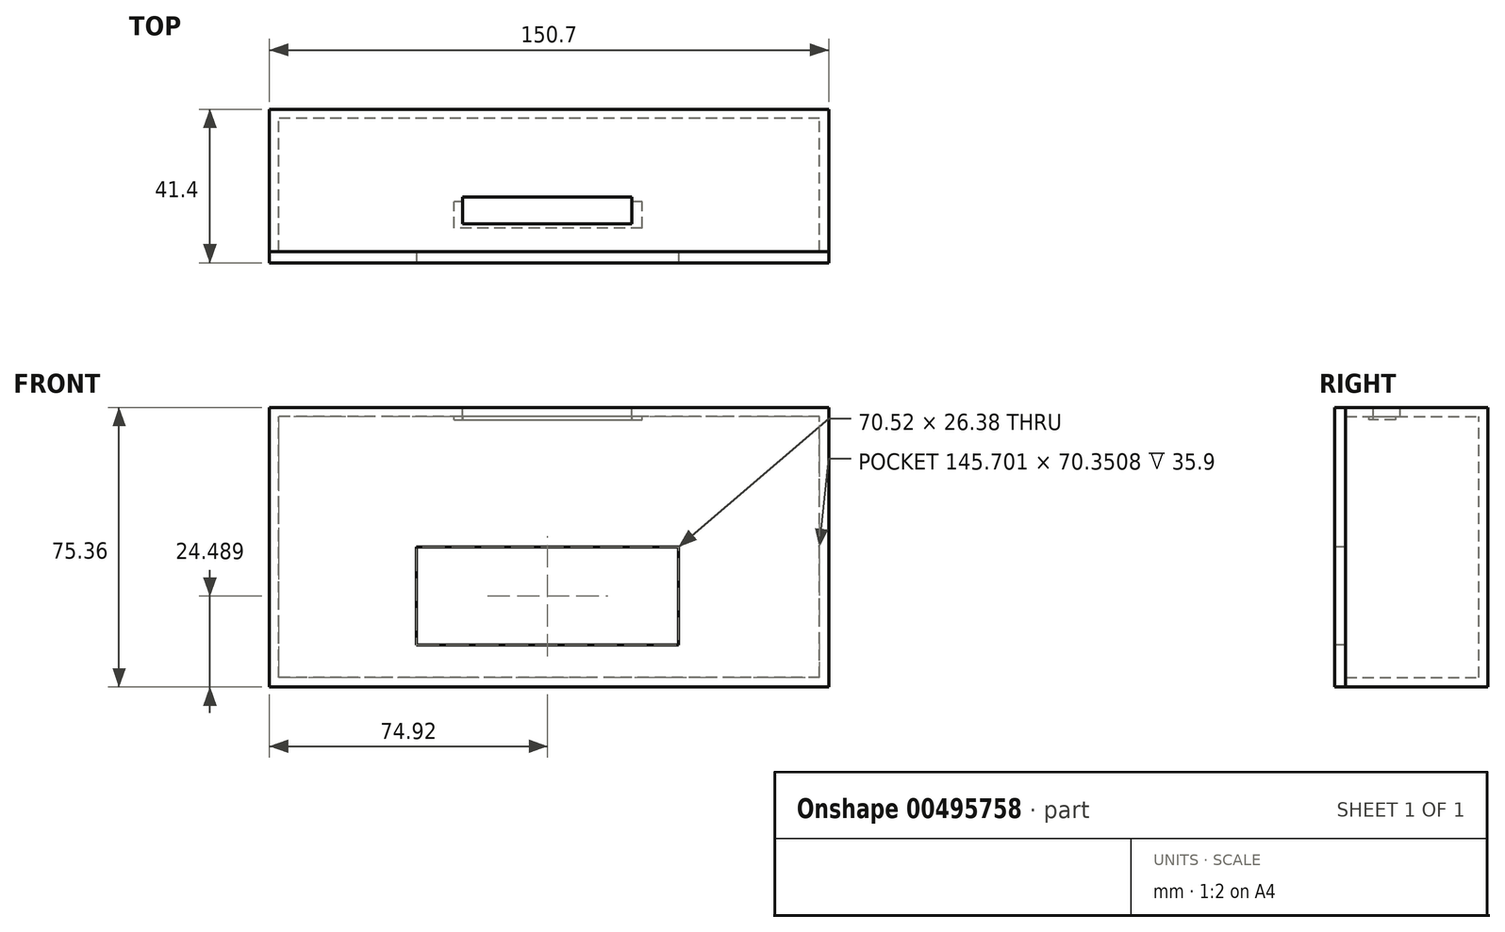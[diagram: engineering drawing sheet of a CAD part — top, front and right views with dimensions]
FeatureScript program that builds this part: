
annotation { "Feature Type Name" : "Feature", "Feature Type Description" : "" }
export const myFeature = defineFeature(function(context is Context, id is Id, definition is map)
    precondition{}
    {
        {
            var Q0;
            Q0=qCreatedBy(makeId("Front.planeOp"),FACE);
            var sketch = newSketch(context, id + "F0", { "sketchPlane" : qUnion([Q0])});
            skLineSegment(sketch, "E0.bottom", {"start": v(75.35, -37.68) * mm, "end": v(-75.35, -37.68) * mm});
            skLineSegment(sketch, "E0.top", {"start": v(75.35, 37.68) * mm, "end": v(-75.35, 37.68) * mm});
            skLineSegment(sketch, "E0.left", {"start": v(75.35, -37.68) * mm, "end": v(75.35, 37.68) * mm});
            skLineSegment(sketch, "E0.right", {"start": v(-75.35, -37.68) * mm, "end": v(-75.35, 37.68) * mm});
            skPoint(sketch, "E0.middle", {"position": v(0, 0) * mm});
            skSolve(sketch);
        }
        {
            var Q0;
            Q0 = qSketchRegion(id + "F0", true);
            extrude(context, id + "F1", {"entities" : qUnion([Q0]), "depth" : 38.4 * mm});
        }
        {
            var Q0;
            Q0=makeQuery(id+"F1.opExtrude","CAP_FACE",FACE,{"disambiguationData":[OSD([sQuery(id+"F0.wireOp",EDGE,"E0.bottom"),sQuery(id+"F0.wireOp",EDGE,"E0.top"),sQuery(id+"F0.wireOp",EDGE,"E0.left"),sQuery(id+"F0.wireOp",EDGE,"E0.right")])],"isStart":false});
            shell(context, id + "F2", {"entities" : qUnion([Q0]), "thickness" : 2.5 * mm});
        }
        {
            var Q0;
            Q0=makeQuery(id+"F1.opExtrude","CAP_FACE",FACE,{"disambiguationData":[OSD([sQuery(id+"F0.wireOp",EDGE,"E0.bottom"),sQuery(id+"F0.wireOp",EDGE,"E0.top"),sQuery(id+"F0.wireOp",EDGE,"E0.left"),sQuery(id+"F0.wireOp",EDGE,"E0.right")])],"isStart":false});
            var sketch = newSketch(context, id + "F3", { "sketchPlane" : qUnion([Q0])});
            skLineSegment(sketch, "E1.bottom", {"start": v(-75.35, 37.68) * mm, "end": v(75.35, 37.68) * mm});
            skLineSegment(sketch, "E1.top", {"start": v(-75.35, -37.68) * mm, "end": v(75.35, -37.68) * mm});
            skLineSegment(sketch, "E1.left", {"start": v(-75.35, 37.68) * mm, "end": v(-75.35, -37.68) * mm});
            skLineSegment(sketch, "E1.right", {"start": v(75.35, 37.68) * mm, "end": v(75.35, -37.68) * mm});
            skSolve(sketch);
        }
        {
            var Q0;
            Q0 = qSketchRegion(id + "F3", true);
            extrude(context, id + "F4", {"entities" : qUnion([Q0]), "depth" : 3 * mm});
        }
        {
            var Q0;
            Q0=makeQuery(id+"F4.opExtrude","CAP_FACE",FACE,{"disambiguationData":[OSD([sQuery(id+"F3.wireOp",EDGE,"E1.bottom"),sQuery(id+"F3.wireOp",EDGE,"E1.top"),sQuery(id+"F3.wireOp",EDGE,"E1.left"),sQuery(id+"F3.wireOp",EDGE,"E1.right")])],"isStart":false});
            var sketch = newSketch(context, id + "F5", { "sketchPlane" : qUnion([Q0])});
            skLineSegment(sketch, "E2.bottom", {"start": v(-35.69, 0) * mm, "end": v(34.83, 0) * mm});
            skLineSegment(sketch, "E2.top", {"start": v(-35.69, -26.38) * mm, "end": v(34.83, -26.38) * mm});
            skLineSegment(sketch, "E2.left", {"start": v(-35.69, 0) * mm, "end": v(-35.69, -26.38) * mm});
            skLineSegment(sketch, "E2.right", {"start": v(34.83, 0) * mm, "end": v(34.83, -26.38) * mm});
            skSolve(sketch);
        }
        {
            var Q0;
            Q0 = qSketchRegion(id + "F5", true);
            extrude(context, id + "F6", {"entities" : qUnion([Q0]), "operationType" : NewBodyOperationType.REMOVE, "oppositeDirection" : true, "depth" : 12 * mm});
        }
        {
            var Q0;
            Q0=makeQuery(id+"F1.opExtrude","SWEPT_FACE",FACE,{"disambiguationData":[OSD([sQuery(id+"F0.wireOp",EDGE,"E0.top")])]});
            var sketch = newSketch(context, id + "F7", { "sketchPlane" : qUnion([Q0])});
            skLineSegment(sketch, "E3.bottom", {"start": v(-25.64, -24.93) * mm, "end": v(25.07, -24.93) * mm});
            skLineSegment(sketch, "E3.top", {"start": v(-25.64, -32) * mm, "end": v(25.07, -32) * mm});
            skLineSegment(sketch, "E3.left", {"start": v(-25.64, -24.93) * mm, "end": v(-25.64, -32) * mm});
            skLineSegment(sketch, "E3.right", {"start": v(25.07, -24.93) * mm, "end": v(25.07, -32) * mm});
            skSolve(sketch);
        }
        {
            var Q0;
            Q0=makeQuery(id+"F7.imprint","IMPRINT",FACE,{"disambiguationData":[TD([[makeQuery(id+"F7.imprint","IMPRINT",EDGE,{"derivedFrom":sQuery(id+"F7.wireOp",EDGE,"E3.bottom")}),-1.0]])]});
            extrude(context, id + "F8", {"entities" : qUnion([Q0]), "operationType" : NewBodyOperationType.ADD, "oppositeDirection" : true, "depth" : 3.3 * mm});
        }
        {
            var Q0;
            Q0=makeQuery(id+"F1.opExtrude","SWEPT_FACE",FACE,{"disambiguationData":[OSD([sQuery(id+"F0.wireOp",EDGE,"E0.top")])]});
            var sketch = newSketch(context, id + "F9", { "sketchPlane" : qUnion([Q0])});
            skLineSegment(sketch, "E4.bottom", {"start": v(-23.34, -23.65) * mm, "end": v(22.24, -23.65) * mm});
            skLineSegment(sketch, "E4.top", {"start": v(-23.34, -30.96) * mm, "end": v(22.24, -30.96) * mm});
            skLineSegment(sketch, "E4.left", {"start": v(-23.34, -23.65) * mm, "end": v(-23.34, -30.96) * mm});
            skLineSegment(sketch, "E4.right", {"start": v(22.24, -23.65) * mm, "end": v(22.24, -30.96) * mm});
            skSolve(sketch);
        }
        {
            var Q0;
            Q0 = qSketchRegion(id + "F9", true);
            extrude(context, id + "F10", {"entities" : qUnion([Q0]), "operationType" : NewBodyOperationType.REMOVE, "oppositeDirection" : true, "depth" : 30.7 * mm});
        }
    });
